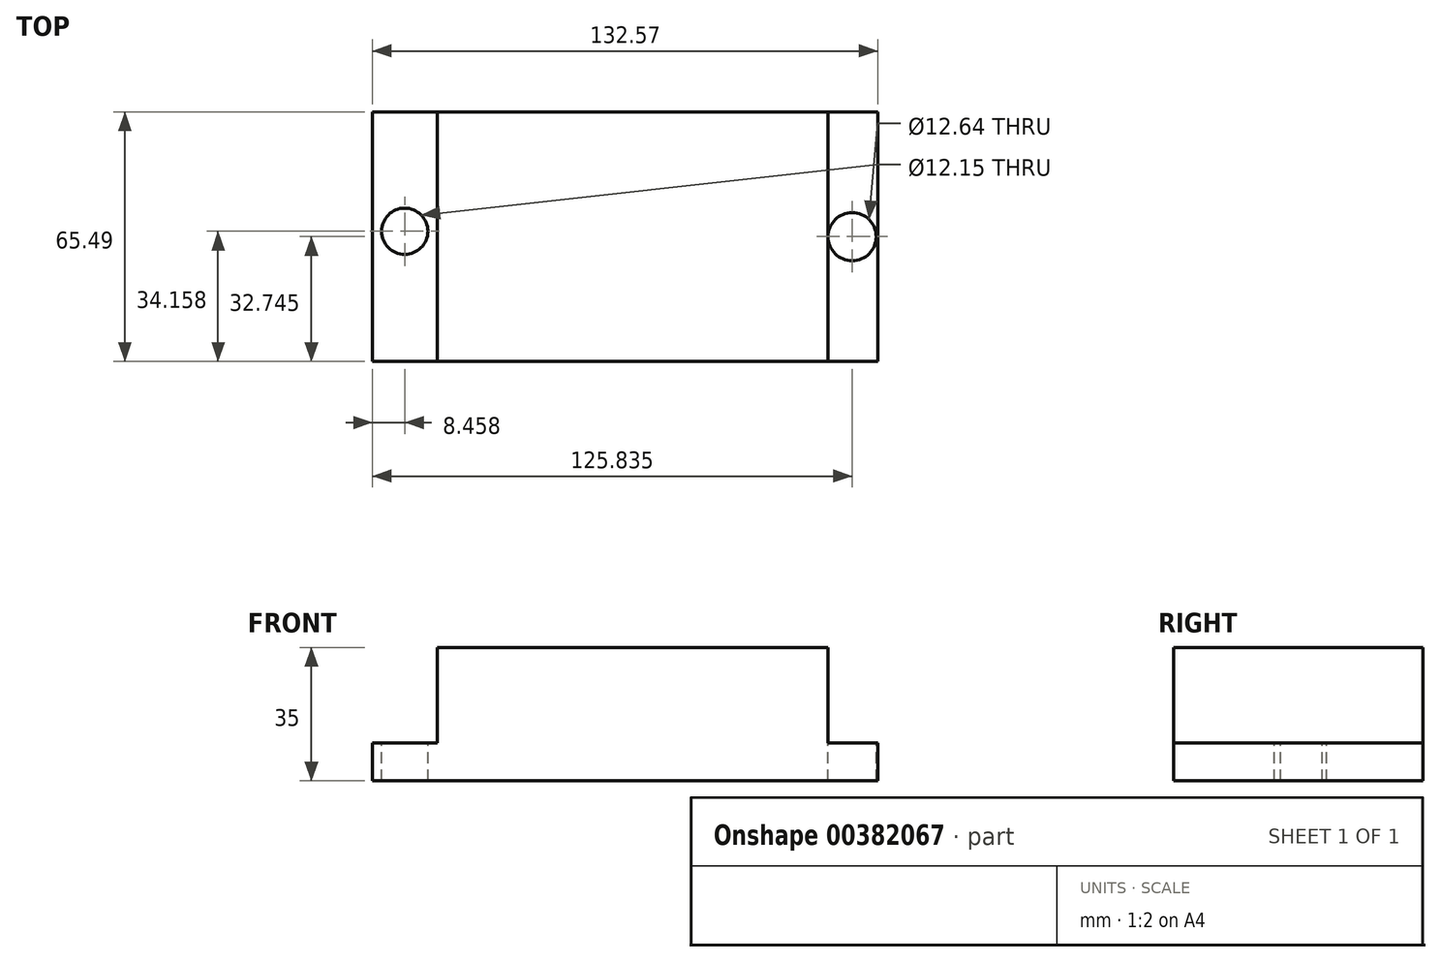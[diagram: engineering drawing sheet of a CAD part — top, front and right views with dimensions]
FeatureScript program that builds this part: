
annotation { "Feature Type Name" : "Feature", "Feature Type Description" : "" }
export const myFeature = defineFeature(function(context is Context, id is Id, definition is map)
    precondition{}
    {
        {
            var Q0;
            Q0=qCreatedBy(makeId("Top.planeOp"),FACE);
            var sketch = newSketch(context, id + "F0", { "sketchPlane" : qUnion([Q0])});
            skLineSegment(sketch, "E0.bottom", {"start": v(-88.25, 65.5) * mm, "end": v(44.32, 65.5) * mm});
            skLineSegment(sketch, "E0.top", {"start": v(-88.25, 0) * mm, "end": v(44.32, 0) * mm});
            skLineSegment(sketch, "E0.left", {"start": v(-88.25, 65.5) * mm, "end": v(-88.25, 0) * mm});
            skLineSegment(sketch, "E0.right", {"start": v(44.32, 65.5) * mm, "end": v(44.32, 0) * mm});
            skSolve(sketch);
        }
        {
            var Q0;
            Q0=makeQuery(id+"F0.imprint","IMPRINT",FACE,{"disambiguationData":[TD([[makeQuery(id+"F0.imprint","IMPRINT",EDGE,{"derivedFrom":sQuery(id+"F0.wireOp",EDGE,"E0.bottom")}),-1.0]])]});
            extrude(context, id + "F1", {"entities" : qUnion([Q0]), "depth" : 35 * mm});
        }
        {
            var Q0;
            Q0=makeQuery(id+"F1.opExtrude","CAP_FACE",FACE,{"disambiguationData":[OSD([sQuery(id+"F0.wireOp",EDGE,"E0.bottom"),sQuery(id+"F0.wireOp",EDGE,"E0.top"),sQuery(id+"F0.wireOp",EDGE,"E0.left"),sQuery(id+"F0.wireOp",EDGE,"E0.right")])],"isStart":false});
            var sketch = newSketch(context, id + "F2", { "sketchPlane" : qUnion([Q0])});
            skLineSegment(sketch, "E1", {"start": v(31.26, 0) * mm, "end": v(31.26, 65.5) * mm});
            skLineSegment(sketch, "E2", {"start": v(-71.24, 0) * mm, "end": v(-71.24, 65.5) * mm});
            skSolve(sketch);
        }
        {
            var Q0;
            {var subQ0=sQuery(id+"F2.wireOp",EDGE,"E1");Q0=makeQuery(id+"F2.imprint","IMPRINT",FACE,{"disambiguationData":[TD([[makeQuery(id+"F2.imprint","IMPRINT",EDGE,{"derivedFrom":subQ0}),-1.0]])]});}
            var Q1;
            {var subQ0=sQuery(id+"F2.wireOp",EDGE,"E2");Q1=makeQuery(id+"F2.imprint","IMPRINT",FACE,{"disambiguationData":[TD([[makeQuery(id+"F2.imprint","IMPRINT",EDGE,{"derivedFrom":subQ0}),1.0]])]});}
            extrude(context, id + "F3", {"entities" : qUnion([Q0, Q1]), "operationType" : NewBodyOperationType.REMOVE, "oppositeDirection" : true, "depth" : 25 * mm});
        }
        {
            var Q0;
            Q0=makeQuery(id+"F3.boolean.opBoolean","COPY",FACE,{"derivedFrom":makeQuery(id+"F3.opExtrude","CAP_FACE",FACE,{"disambiguationData":[OSD([sQuery(id+"F0.wireOp",EDGE,"E0.bottom"),sQuery(id+"F0.wireOp",EDGE,"E0.top"),sQuery(id+"F0.wireOp",EDGE,"E0.right"),sQuery(id+"F2.wireOp",EDGE,"E1")])],"isStart":false})});
            var sketch = newSketch(context, id + "F4", { "sketchPlane" : qUnion([Q0])});
            skCircle(sketch, "E3", {"center": v(37.58, 32.75) * mm, "radius": 6.32 * mm});
            skPoint(sketch, "E3.centerSnap0", {"position": v(44.32, 32.75) * mm});
            skSolve(sketch);
        }
        {
            var Q0;
            Q0=makeQuery(id+"F4.imprint","IMPRINT",FACE,{"disambiguationData":[TD([[makeQuery(id+"F4.imprint","IMPRINT",EDGE,{"derivedFrom":sQuery(id+"F4.wireOp",EDGE,"E3")}),1.0]])]});
            extrude(context, id + "F5", {"entities" : qUnion([Q0]), "operationType" : NewBodyOperationType.REMOVE, "endBound" : BoundingType.THROUGH_ALL, "oppositeDirection" : true, "depth" : 25 * mm});
        }
        {
            var Q0;
            Q0=makeQuery(id+"F3.boolean.opBoolean","COPY",FACE,{"derivedFrom":makeQuery(id+"F3.opExtrude","CAP_FACE",FACE,{"disambiguationData":[OSD([sQuery(id+"F0.wireOp",EDGE,"E0.bottom"),sQuery(id+"F0.wireOp",EDGE,"E0.top"),sQuery(id+"F0.wireOp",EDGE,"E0.left"),sQuery(id+"F2.wireOp",EDGE,"E2")])],"isStart":false})});
            var sketch = newSketch(context, id + "F6", { "sketchPlane" : qUnion([Q0])});
            skCircle(sketch, "E4", {"center": v(-79.8, 34.16) * mm, "radius": 6.07 * mm});
            skSolve(sketch);
        }
        {
            var Q0;
            Q0=makeQuery(id+"F6.imprint","IMPRINT",FACE,{"disambiguationData":[TD([[makeQuery(id+"F6.imprint","IMPRINT",EDGE,{"derivedFrom":sQuery(id+"F6.wireOp",EDGE,"E4")}),1.0]])]});
            extrude(context, id + "F7", {"entities" : qUnion([Q0]), "operationType" : NewBodyOperationType.REMOVE, "oppositeDirection" : true, "depth" : 25 * mm});
        }
    });
